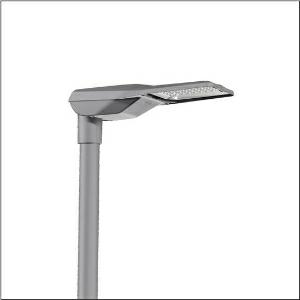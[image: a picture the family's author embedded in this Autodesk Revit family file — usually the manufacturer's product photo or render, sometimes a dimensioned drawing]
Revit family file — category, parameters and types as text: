
# Revit family: streetlight_sl_21_iq_mini___st0_5a_5xe2b31g08hb_4c73
name_source: partatom
category: Lighting Fixtures
units: mm (PartAtom-declared; Revit-internal decimal feet)

## family parameters
Cut with Voids When Loaded = No
Host = Face
Light Source = No
Part Type = Normal
Room Calculation Point = No
Round Connector Dimension = Use Diameter
Shared = No

## types (1)
- --- (1 x LED, 9450 lm, 70.9 W, 3000K)
    Apparent Load = 71 VA
    CIE Flux Codes = 41 75 97 100 100
    Color Rendering = 70
    Color Temperature = 3000K
    Default Elevation = 1800 mm
    Description = Streetlight SL 21 iQ mini, mast luminaire, primary light control with lens, of PMMA, primary optical cover: cover, of toughened safety glass, transparent, light distribution: ST0.5a, light emission: direct distribution, primary light characteristic: asymmetric, installation type: post-top, side-entry, LED, High Power LED, rated luminous flux: 9.450lm, luminous efficacy: 133lm/W, light colour: 730, colour temperature: 3000K, control gear: iQ Street-Remote, control: Street-Remote, Auto-Match, Temp-Guard, Lumen-Switch, Night-Set, Smart-Wire, Light-Fading, Desk-Remote (wireless, voltage-free reading and setting of iQ features in the workshop via application-optimized NFC function/RFID function), optimised constant luminous flux control (CLO 2.0), pre-setting: linear dimming characteristic, mains connection: 220..240V, AC, 50/60Hz, start of lifetime: 71W, end of service life: 75W, reduction: 31W, luminaire housing, of diecast aluminium, powder-coated, SITECO metallic grey (DB 702S), corrosivity category C5 high according to DIN EN ISO 12944, please order mast flange separately, inclination adjustable: 0°, 5°, 10°, 15°, sealing non-destructively replaceable, multi-level sealing system, length: 628mm, width: 235mm, height: 110mm, mast flange for spigot size: 42mm (side-entry): 5XC10008XM4, 60/48mm (side-entry/post-top): 5XC10108XM2, 76/60mm (side-entry/post-top): 5XC10108XM1, mounting height: 4..8m, protection rating (complete): IP66, insulation class (complete): insulation class II (safety insulation), certification: CE, ENEC, ENEC+, VDE, impact resistance: IK10, permissible operating ambient temperature for outdoor applications: -40..+50°C, standard-compliant lighting for roads and squares, packaging unit: 1 piece

Light Distribution: ST0.5a
    Height = 110 mm
    Lamp = 1 x LED
    Lamp Light Flux = 9450 lm
    Lamp Power = 70.9 W
    Lamp count = 1
    Length = 625 mm
    Luminous efficacy = 133 lm/W
    Manufacturer = Siteco
    ModVariant = No
    Model = 5XE2B31G08HB
    Number of Poles = 1
    OnlyDefault = Yes
    Power Factor = 1
    Product Name = Streetlight SL 21 iQ mini | ST0.5a
    Product group = mast luminaire | pylon top
    ProductGroupID = 6100
    Protection Class = Protection class II
    Protection Degree = IP 66
    RLX_Detail_Level = 1
    RLX_Emergency_Light_Flux = 0 lm
    RLX_Emergency_Type = 0
    RLX_Emergency_Type_DB = No
    RlxData = <blob elided: 37273 chars, md5=426eb759>
    Socket = socket
    Standby Power = 0 W
    System Light Flux = 9450 lm
    System Power = 71 W
    Type Comments = factory setting: luminous flux: 100 % | dim-lin: 254 | 711 mA
    Type Image = l_1003519.jpg
    URL = http://relux.com
    VarID = @adj_158059
    Voltage = 0 V
    Weight = 0.00 kg
    Width = 234 mm

## geometry (parser evidence)
native form markers: Blend x4, Sweep x12
no freeform markers — native parametric forms only
